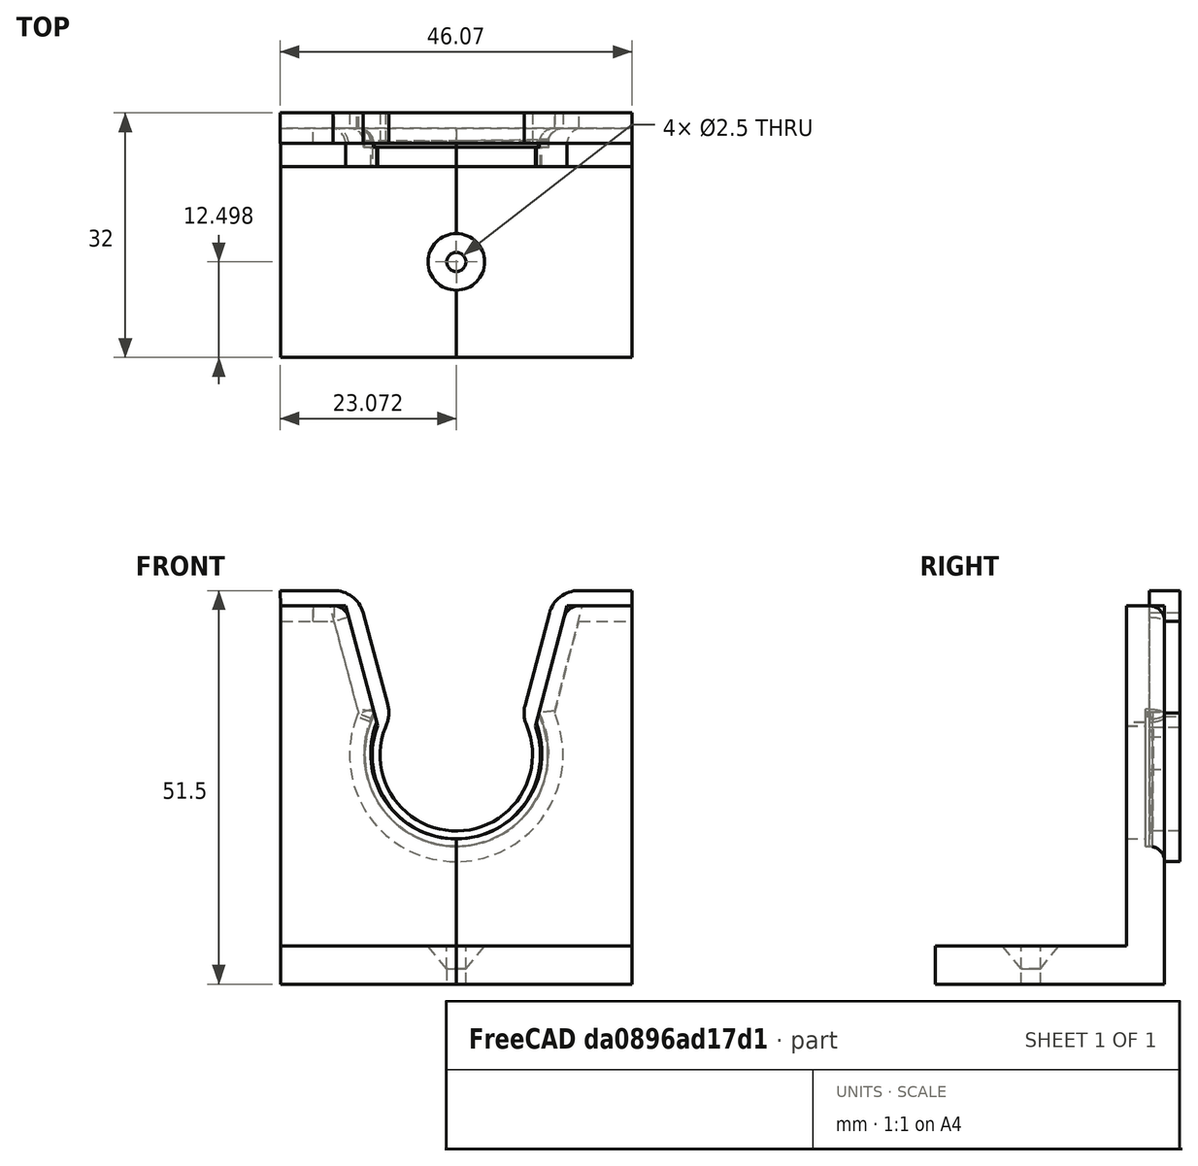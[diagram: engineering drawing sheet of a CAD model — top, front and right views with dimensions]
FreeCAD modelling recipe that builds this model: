
FCSTD DOCUMENT  (FreeCAD 0.20R29177 +233 (Git))
Label: Borotvapamacs.Tarto
License: All rights reserved
LicenseURL: http://en.wikipedia.org/wiki/All_rights_reserved
objects: Part::Part2DObjectPython×20, Part::Extrusion×14, Part::Cut×13, Part::Feature×9, PartDesign::FeatureBase×3, PartDesign::AdditivePipe×3, PartDesign::Body×3, Part::FeaturePython×2, PartDesign::ShapeBinder×2, Part::MultiFuse×2, Part::Refine×2
note: 76 computed .brp shape members not serialized (recipe doc carries the construction recipe); baked Part::Feature solids carry a one-line shape summary decoded from their .brp

FEATURE [Part::FeaturePython] Cut010009009_child0  label="Cut010009009.0"  # WARN: FeaturePython — macro-defined, semantics opaque (R4)
  FilterType = 1
  Invert = false
  OverrideMaxVal = 0
  WindowFrom = 80
  WindowTo = 100
  items = 0
FEATURE [Part::Part2DObjectPython] Rectangle  # Draft 2D object (typed FeaturePython)
  ChamferSize = 0
  Columns = 1
  FilletRadius = 0
  Height = 49.5
  Length = 30
  MakeFace = true
  Placement = pos=(-148.148,-554.302,-6) rot=(0.57735,0.57735,0.57735;2.0944rad)
  Rows = 1
  Support = -> [Cut010009009_child0]
FEATURE [Part::FeaturePython] Slice001  label="ToDelete"  # WARN: FeaturePython — macro-defined, semantics opaque (R4)
  Base = -> Cut010009009_child0
  Mode = 1
  Tolerance = 0
  Tools = -> [Rectangle]
FEATURE [Part::Part2DObjectPython] Rectangle002  # Draft 2D object (typed FeaturePython)
  ChamferSize = 0
  Columns = 1
  FilletRadius = 0
  Height = 49.5
  Length = 30
  MakeFace = true
  Placement = pos=(-125.148,-554.302,-6) rot=(0.57735,0.57735,0.57735;2.0944rad)
  Rows = 1
  Support = -> [Slice001]
FEATURE [Part::Extrusion] Extrusion
  Base = -> Rectangle002
  Dir = (-46,0,0)
  DirMode = 0
  FaceMakerClass = Part::FaceMakerBullseye
  LengthFwd = 0
  LengthRev = 0
  Solid = true
  Symmetric = false
FEATURE [Part::Part2DObjectPython] Rectangle003  # Draft 2D object (typed FeaturePython)
  ChamferSize = 0
  Columns = 1
  FilletRadius = 0
  Height = 44.5
  Length = 25
  MakeFace = true
  Placement = pos=(-125.148,-554.302,-1) rot=(0.57735,0.57735,0.57735;2.0944rad)
  Rows = 1
FEATURE [Part::Extrusion] Extrusion001
  Base = -> Rectangle003
  Dir = (-46,0,0)
  DirMode = 0
  FaceMakerClass = Part::FaceMakerBullseye
  LengthFwd = 0
  LengthRev = 0
  Solid = true
  Symmetric = false
FEATURE [Part::Cut] Cut
  Base = -> Extrusion
  Tool = -> Extrusion001
FEATURE [Part::Part2DObjectPython] Circle  # Draft 2D object (typed FeaturePython)
  FirstAngle = 0
  LastAngle = 0
  MakeFace = true
  Placement = pos=(-148.148,-529.302,24) rot=(1,0,0;1.5708rad)
  Radius = 11
FEATURE [Part::Extrusion] Extrusion002
  Base = -> Circle
  Dir = (2e-16,5,-1.1e-15)
  DirMode = 0
  FaceMakerClass = Part::FaceMakerBullseye
  LengthFwd = 0
  LengthRev = 0
  Solid = true
  Symmetric = false
FEATURE [Part::Cut] Cut001
  Base = -> Cut
  Tool = -> Extrusion002
FEATURE [Part::Part2DObjectPython] Wire  # Draft 2D object (typed FeaturePython)
  ChamferSize = 0
  Closed = true
  End = (-133.648,-529.302,43.5)
  FilletRadius = 0
  Length = 82.1577
  MakeFace = true
  Placement = pos=(-137.806,-529.302,27.747) rot=(1,0,0;1.5708rad)
  Points = (4) [(0,0,0),(-20.6512,0.0901061,0),(-24.8421,15.753,0),(4.15786,15.753,0)]
  Start = (-137.806,-529.302,27.747)
  Subdivisions = 0
FEATURE [Part::Extrusion] Extrusion003
  Base = -> Wire
  Dir = (2e-16,5,-1.1e-15)
  DirMode = 0
  FaceMakerClass = Part::FaceMakerBullseye
  LengthFwd = 0
  LengthRev = 0
  Solid = true
  Symmetric = false
FEATURE [Part::Cut] Cut002
  Base = -> Cut001
  Tool = -> Extrusion003
FEATURE [Part::Part2DObjectPython] Circle001  # Draft 2D object (typed FeaturePython)
  FirstAngle = 0
  LastAngle = 0
  MakeFace = true
  Placement = pos=(-148.148,-541.802,-6) rot=(1,0,0;3.14159rad)
  Radius = 1.25
  Support = -> [Slice001]
FEATURE [Part::Part2DObjectPython] Circle002  # Draft 2D object (typed FeaturePython)
  FirstAngle = 0
  LastAngle = 0
  MakeFace = true
  Placement = pos=(-148.148,-524.302,24) rot=(-1,0,0;1.5708rad)
  Radius = 12
FEATURE [Part::Extrusion] Extrusion005
  Base = -> Circle002
  Dir = (-1e-16,-2.5,-6e-16)
  DirMode = 0
  FaceMakerClass = Part::FaceMakerBullseye
  LengthFwd = 0
  LengthRev = 0
  Solid = true
  Symmetric = false
FEATURE [Part::Cut] Cut004
  Base = -> Cut002
  Tool = -> Extrusion005
FEATURE [Part::Part2DObjectPython] Circle003  # Draft 2D object (typed FeaturePython)
  FirstAngle = 0
  LastAngle = 0
  MakeFace = true
  Placement = pos=(-148.148,-541.802,-6) rot=(1,0,0;3.14159rad)
  Radius = 1.25
FEATURE [Part::Extrusion] Extrusion006
  Base = -> Circle003
  Dir = (0,0,5)
  DirMode = 0
  FaceMakerClass = Part::FaceMakerBullseye
  LengthFwd = 0
  LengthRev = 0
  Solid = true
  Symmetric = false
FEATURE [Part::Cut] Cut005
  Base = -> Cut004
  Tool = -> Extrusion006
FEATURE [Part::Part2DObjectPython] Rectangle008  # Draft 2D object (typed FeaturePython)
  ChamferSize = 0
  Columns = 1
  FilletRadius = 0
  Height = 2
  Length = 2
  MakeFace = true
  Placement = pos=(-171.148,-524.302,41.5) rot=(0.57735,-0.57735,-0.57735;2.0944rad)
  Rows = 1
  Support = -> [Cut005]
FEATURE [Part::Part2DObjectPython] Circle005  # Draft 2D object (typed FeaturePython)
  FirstAngle = 0
  LastAngle = 0
  MakeFace = true
  Placement = pos=(-171.148,-526.302,41.5) rot=(0.57735,-0.57735,-0.57735;2.0944rad)
  Radius = 2
FEATURE [Part::Cut] Cut006
  Base = -> Rectangle008
  Tool = -> Circle005
FEATURE [Part::Feature] Wire008
  shape: bbox 46 x 2e-07 x 31.47 mm, 0 faces, 0 solids (baked)
FEATURE [PartDesign::FeatureBase] BaseFeature
FEATURE [PartDesign::ShapeBinder] CopyWire008
  TraceSupport = false
FEATURE [PartDesign::AdditivePipe] AdditivePipe
  AllowMultiFace = false
  AuxilleryCurvelinear = true
  AuxillerySpineTangent = false
  BaseFeature = -> BaseFeature
  Binormal = (0,0,0)
  Mode = 0
  Profile = -> BaseFeature [Face1]
  Spine = -> CopyWire008
  SpineTangent = false
  Transformation = 0
  Transition = 0
FEATURE [PartDesign::Body] Body
  Group = -> [BaseFeature,AdditivePipe,CopyWire008]
  Origin = -> Origin
  Tip = -> AdditivePipe
FEATURE [Part::Feature] AdditivePipe001
  shape: bbox 46.08 x 4 x 35.47 mm, 33 faces (baked)
FEATURE [Part::Cut] Cut008
  Base = -> Cut005
  Tool = -> AdditivePipe001
FEATURE [Part::Extrusion] Extrusion009
  Base = -> Cut006
  Dir = (4.25,0,0)
  DirMode = 0
  FaceMakerClass = Part::FaceMakerBullseye
  LengthFwd = 0
  LengthRev = 0
  Solid = true
  Symmetric = false
FEATURE [Part::Cut] Cut009
  Base = -> Cut008
  Tool = -> Extrusion009
FEATURE [Part::Part2DObjectPython] Wire009  # Draft 2D object (typed FeaturePython)
  ChamferSize = 0
  Closed = true
  End = (-164.013,-526.302,48.1631)
  FilletRadius = 0
  Length = 18.5521
  MakeFace = true
  Placement = pos=(-164.183,-526.302,43.5) rot=(-1,0,0;1.5708rad)
  Points = (4) [(0,0,0),(1.93203,1.48304,1.13687e-13),(5.73348,0.335399,1.13687e-13),(0.16965,-4.66314,1.13687e-13)]
  Start = (-164.183,-526.302,43.5)
  Subdivisions = 0
FEATURE [Part::Part2DObjectPython] Wire010  # Draft 2D object (typed FeaturePython)
  ChamferSize = 0
  Closed = true
  End = (-132.107,-526.302,43.5)
  FilletRadius = 0
  Length = 19.3995
  MakeFace = true
  Placement = pos=(-134.041,-526.302,42.0104) rot=(-1,0,0;1.5708rad)
  Points = (4) [(0,0,0),(-2.64687,-1.29032,1.13687e-13),(1.83186,-7.69081,1.13687e-13),(1.93378,-1.4896,0)]
  Start = (-134.041,-526.302,42.0104)
  Subdivisions = 0
FEATURE [Part::Extrusion] Extrusion010
  Base = -> Wire010
  Dir = (-7.99e-14,-3,5.73e-14)
  DirMode = 0
  FaceMakerClass = Part::FaceMakerBullseye
  LengthFwd = 0
  LengthRev = 0
  Solid = true
  Symmetric = false
FEATURE [Part::Extrusion] Extrusion011
  Base = -> Wire009
  Dir = (4.21e-14,-3,3.45e-14)
  DirMode = 0
  FaceMakerClass = Part::FaceMakerBullseye
  LengthFwd = 0
  LengthRev = 0
  Solid = true
  Symmetric = false
FEATURE [Part::Cut] Cut010
  Base = -> Cut009
  Tool = -> Extrusion011
FEATURE [Part::Cut] Cut011
  Base = -> Cut010
  Tool = -> Extrusion010
FEATURE [Part::Part2DObjectPython] Wire011  # Draft 2D object (typed FeaturePython)
  ChamferSize = 0
  Closed = true
  End = (-148.148,-538.102,-1)
  FilletRadius = 0
  Length = 9.32331
  MakeFace = true
  Placement = pos=(-148.148,-540.552,-4) rot=(0,0,1;0rad)
  Points = (3) [(0,0,0),(2.84217e-14,0,3),(0,2.45,3)]
  Start = (-148.148,-540.552,-4)
  Subdivisions = 0
FEATURE [Part::Part2DObjectPython] Arc  # Draft 2D object (typed FeaturePython)
  FirstAngle = 0
  LastAngle = 360
  MakeFace = true
  Placement = pos=(-148.148,-541.802,-1) rot=(0,0,1;0rad)
  Radius = 3.7
FEATURE [PartDesign::FeatureBase] BaseFeature001
  BaseFeature = -> Wire011
FEATURE [PartDesign::ShapeBinder] CopyArc
  Placement = pos=(-148.148,-541.802,-1) rot=(0,0,1;0rad)
  TraceSupport = false
FEATURE [PartDesign::AdditivePipe] AdditivePipe002
  AllowMultiFace = false
  AuxilleryCurvelinear = true
  AuxillerySpineTangent = false
  BaseFeature = -> BaseFeature001
  Binormal = (0,0,0)
  Mode = 0
  Profile = -> Wire011
  Spine = -> CopyArc [Edge1]
  SpineTangent = false
  Transformation = 0
  Transition = 0
FEATURE [PartDesign::Body] Body001
  BaseFeature = -> Wire011
  Group = -> [BaseFeature001,AdditivePipe002,CopyArc]
  Origin = -> Origin001
  Tip = -> AdditivePipe002
FEATURE [Part::Part2DObjectPython] Circle006  # Draft 2D object (typed FeaturePython)
  FirstAngle = 0
  LastAngle = 0
  MakeFace = true
  Placement = pos=(-148.148,-541.802,-1) rot=(0,0,1;0rad)
  Radius = 3.7
  Support = -> [Slice001]
FEATURE [Part::Cut] Cut012  label="Borotva.Pamacs.Tarto"
  Base = -> Cut011
  Tool = -> AdditivePipe002
FEATURE [Part::Part2DObjectPython] Circle007  # Draft 2D object (typed FeaturePython)
  FirstAngle = 0
  LastAngle = 0
  MakeFace = true
  Placement = pos=(-148.148,-541.802,-6) rot=(1,0,0;3.14159rad)
  Radius = 1.25
  Support = -> [Cut012]
FEATURE [Part::Extrusion] Extrusion012
  Base = -> Circle007
  Dir = (0,0,5)
  DirMode = 0
  FaceMakerClass = Part::FaceMakerBullseye
  LengthFwd = 0
  LengthRev = 0
  Solid = true
  Symmetric = false
FEATURE [Part::Part2DObjectPython] Wire012  # Draft 2D object (typed FeaturePython)
  ChamferSize = 0
  Closed = true
  End = (-144.448,-541.802,-1)
  FilletRadius = 0
  Length = 9.32331
  MakeFace = true
  Placement = pos=(-146.898,-541.802,-1) rot=(1,0,0;3.14159rad)
  Points = (3) [(0,0,0),(0,0,3),(2.45,0,4.44089e-16)]
  Start = (-146.898,-541.802,-1)
  Subdivisions = 0
FEATURE [Part::Part2DObjectPython] Arc001  # Draft 2D object (typed FeaturePython)
  FirstAngle = 0
  LastAngle = 360
  MakeFace = true
  Placement = pos=(-148.148,-541.802,-1) rot=(0,0,1;0rad)
  Radius = 3.7
FEATURE [PartDesign::FeatureBase] BaseFeature002
  BaseFeature = -> Wire012
FEATURE [PartDesign::AdditivePipe] AdditivePipe003
  AllowMultiFace = false
  AuxilleryCurvelinear = true
  AuxillerySpineTangent = false
  BaseFeature = -> BaseFeature002
  Binormal = (0,0,0)
  Mode = 0
  Profile = -> Wire012
  Spine = -> Arc001 [Edge1]
  SpineTangent = false
  Transformation = 0
  Transition = 0
FEATURE [PartDesign::Body] Body002
  BaseFeature = -> Wire012
  Group = -> [BaseFeature002,AdditivePipe003]
  Origin = -> Origin002
  Tip = -> AdditivePipe003
FEATURE [Part::MultiFuse] Fusion
  Shapes = -> [Extrusion012,AdditivePipe003]
FEATURE [Part::Feature] Face
  shape: bbox 1.932 x 2e-07 x 1.483 mm, 1 faces, 0 solids (baked)
FEATURE [Part::Extrusion] Extrusion013
  Base = -> Face
  Dir = (4.22e-14,-3,3.52e-14)
  DirMode = 0
  FaceMakerClass = Part::FaceMakerBullseye
  LengthFwd = 0
  LengthRev = 0
  Solid = true
  Symmetric = false
FEATURE [Part::Feature] Face001
  shape: bbox 1.934 x 2e-07 x 1.49 mm, 1 faces, 0 solids (baked)
FEATURE [Part::Extrusion] Extrusion014
  Base = -> Face001
  Dir = (-7.98e-14,-3,5.8e-14)
  DirMode = 0
  FaceMakerClass = Part::FaceMakerBullseye
  LengthFwd = 0
  LengthRev = 0
  Solid = true
  Symmetric = false
FEATURE [Part::MultiFuse] Fusion001
  Shapes = -> [Extrusion014,Cut012,Extrusion013]
FEATURE [Part::Feature] Fusion001_solid  label="Fusion001 (Solid)"
  shape: bbox 46 x 30 x 49.5 mm, 36 faces (baked)
FEATURE [Part::Refine] Fusion001001
  Source = -> Fusion001
FEATURE [Part::Feature] Face002
  shape: bbox 0.1617 x 3e-07 x 0.9286 mm, 1 faces, 0 solids (baked)
FEATURE [Part::Extrusion] Extrusion015
  Base = -> Face002
  Dir = (0,-0.5,0)
  DirMode = 0
  FaceMakerClass = Part::FaceMakerBullseye
  LengthFwd = 0
  LengthRev = 0
  Solid = true
  Symmetric = false
FEATURE [Part::Cut] Cut013
  Base = -> Fusion001001
  Tool = -> Extrusion015
FEATURE [Part::Feature] Face003
  shape: bbox 0.1692 x 3e-07 x 0.9703 mm, 1 faces, 0 solids (baked)
FEATURE [Part::Extrusion] Extrusion016
  Base = -> Face003
  Dir = (0,-0.5,0)
  DirMode = 0
  FaceMakerClass = Part::FaceMakerBullseye
  LengthFwd = 0
  LengthRev = 0
  Solid = true
  Symmetric = false
FEATURE [Part::Cut] Cut014
  Base = -> Cut013
  Tool = -> Extrusion016
FEATURE [Part::Part2DObjectPython] Line  # Draft 2D object (typed FeaturePython)
  Area = 0
  ChamferSize = 0
  Closed = false
  End = (-171.148,-526.302,-23.383)
  FilletRadius = 0
  Length = 66.883
  MakeFace = true
  Placement = pos=(-171.148,-526.302,43.5) rot=(0.57735,-0.57735,-0.57735;2.0944rad)
  Points = (2) [(0,0,0),(0,-66.883,0)]
  Start = (-171.148,-526.302,43.5)
  Subdivisions = 0
FEATURE [Part::Part2DObjectPython] Line001  # Draft 2D object (typed FeaturePython)
  Area = 0
  ChamferSize = 0
  Closed = false
  End = (-171.148,-526.302,41.5)
  FilletRadius = 0
  Length = 2
  MakeFace = true
  Placement = pos=(-171.148,-524.302,41.5) rot=(0.57735,-0.57735,-0.57735;2.0944rad)
  Points = (2) [(0,0,0),(2,0,-2.84217e-14)]
  Start = (-171.148,-524.302,41.5)
  Subdivisions = 0
FEATURE [Part::Feature] GrExplode_Slice002_solid  label="Exploded Slice002 (Solid)"
  shape: bbox 46 x 30 x 49.5 mm, 34 faces (baked)
FEATURE [Part::Feature] Cut014_solid  label="Cut014 (Solid)"
  shape: bbox 46 x 30 x 49.5 mm, 34 faces (baked)
FEATURE [Part::Refine] Cut014_solid001  label="Cut014 (Solid)001"
  Source = -> Cut014_solid
